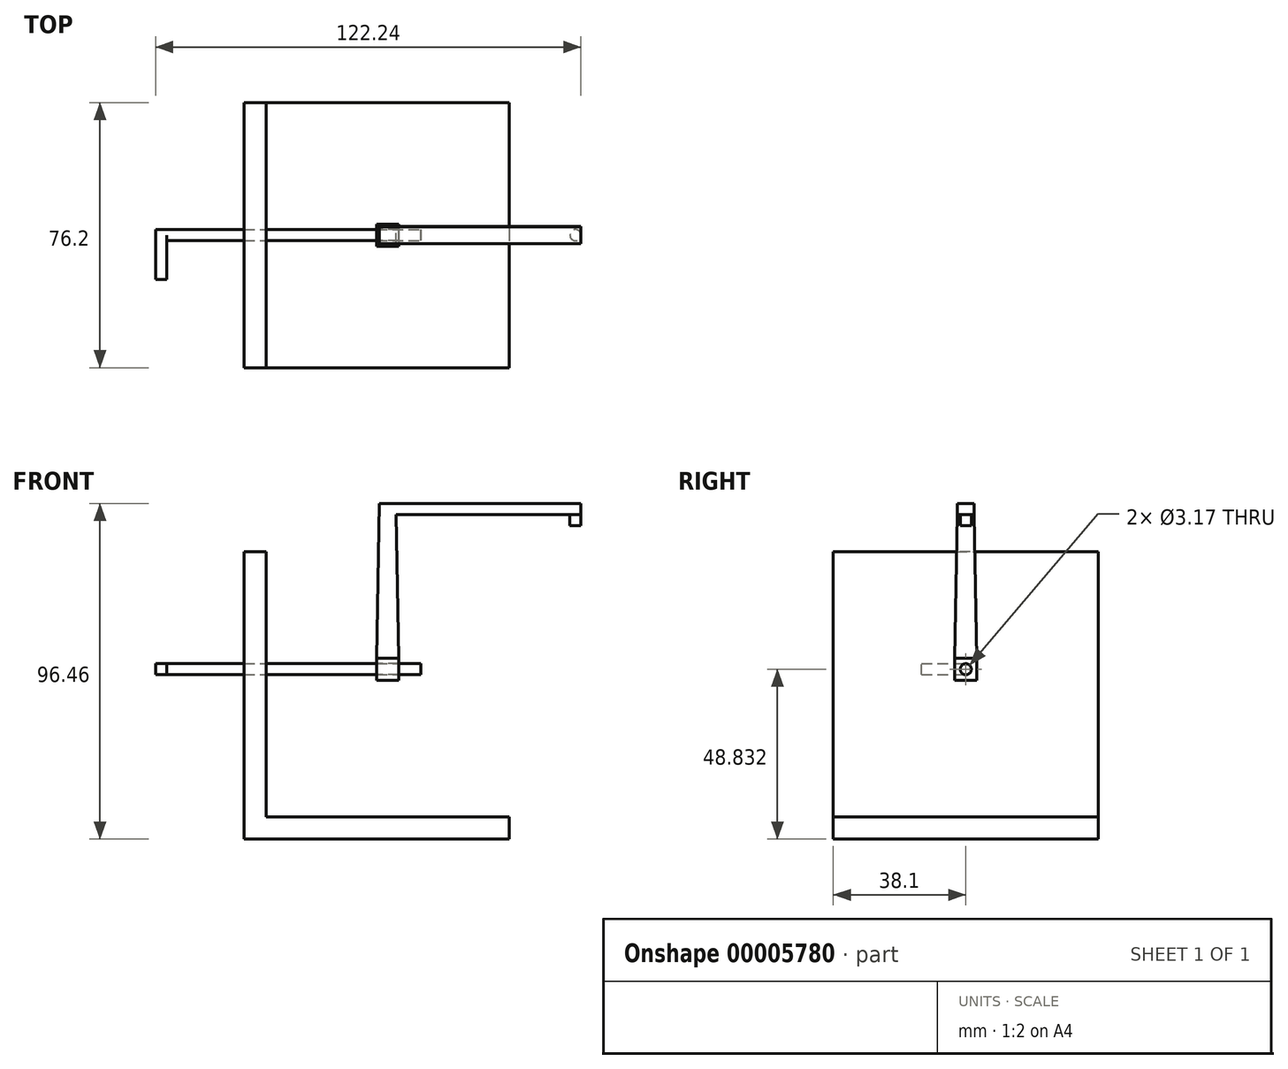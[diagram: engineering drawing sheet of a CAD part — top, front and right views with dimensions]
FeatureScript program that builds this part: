
annotation { "Feature Type Name" : "Feature", "Feature Type Description" : "" }
export const myFeature = defineFeature(function(context is Context, id is Id, definition is map)
    precondition{}
    {
        {
            var Q0;
            Q0=qCreatedBy(makeId("Top.planeOp"),FACE);
            var sketch = newSketch(context, id + "F0", { "sketchPlane" : qUnion([Q0])});
            skLineSegment(sketch, "E0.bottom", {"start": v(38.1, 38.1) * mm, "end": v(-38.1, 38.1) * mm});
            skLineSegment(sketch, "E0.top", {"start": v(38.1, -38.1) * mm, "end": v(-38.1, -38.1) * mm});
            skLineSegment(sketch, "E0.left", {"start": v(38.1, 38.1) * mm, "end": v(38.1, -38.1) * mm});
            skLineSegment(sketch, "E0.right", {"start": v(-38.1, 38.1) * mm, "end": v(-38.1, -38.1) * mm});
            skPoint(sketch, "E0.middle", {"position": v(0, 0) * mm});
            skSolve(sketch);
        }
        {
            var Q0;
            Q0=makeQuery(id+"F0.imprint","IMPRINT",FACE,{"disambiguationData":[TD([[makeQuery(id+"F0.imprint","IMPRINT",EDGE,{"derivedFrom":sQuery(id+"F0.wireOp",EDGE,"E0.bottom")}),1.0]])]});
            extrude(context, id + "F1", {"entities" : qUnion([Q0]), "depth" : 6.35 * mm});
        }
        {
            var Q0;
            Q0=makeQuery(id+"F1.opExtrude","CAP_FACE",FACE,{"disambiguationData":[OSD([sQuery(id+"F0.wireOp",EDGE,"E0.bottom"),sQuery(id+"F0.wireOp",EDGE,"E0.top"),sQuery(id+"F0.wireOp",EDGE,"E0.left"),sQuery(id+"F0.wireOp",EDGE,"E0.right")])],"isStart":false});
            var sketch = newSketch(context, id + "F2", { "sketchPlane" : qUnion([Q0])});
            skLineSegment(sketch, "E1.bottom", {"start": v(-38.1, -38.1) * mm, "end": v(-31.75, -38.1) * mm});
            skLineSegment(sketch, "E1.top", {"start": v(-38.1, 38.1) * mm, "end": v(-31.75, 38.1) * mm});
            skLineSegment(sketch, "E1.left", {"start": v(-38.1, -38.1) * mm, "end": v(-38.1, 38.1) * mm});
            skLineSegment(sketch, "E1.right", {"start": v(-31.75, -38.1) * mm, "end": v(-31.75, 38.1) * mm});
            skSolve(sketch);
        }
        {
            var Q0;
            Q0=makeQuery(id+"F2.imprint","IMPRINT",FACE,{"disambiguationData":[TD([[makeQuery(id+"F2.imprint","IMPRINT",EDGE,{"derivedFrom":sQuery(id+"F2.wireOp",EDGE,"E1.bottom")}),-1.0]])]});
            extrude(context, id + "F3", {"entities" : qUnion([Q0]), "operationType" : NewBodyOperationType.ADD, "depth" : 76.2 * mm});
        }
        {
            var Q0;
            Q0=makeQuery(id+"F3.boolean.opBoolean","MERGE",FACE,{"derivedFrom":[makeQuery(id+"F1.opExtrude","SWEPT_FACE",FACE,{"disambiguationData":[OSD([sQuery(id+"F0.wireOp",EDGE,"E0.right")])]}),makeQuery(id+"F3.opExtrude","SWEPT_FACE",FACE,{"disambiguationData":[OSD([sQuery(id+"F2.wireOp",EDGE,"E1.left")])]})]});
            var sketch = newSketch(context, id + "F4", { "sketchPlane" : qUnion([Q0])});
            skCircle(sketch, "E2", {"center": v(0, 48.83) * mm, "radius": 1.59 * mm});
            skPoint(sketch, "E2.centerSnap0", {"position": v(0, 82.55) * mm});
            skSolve(sketch);
        }
        {
            var Q0;
            Q0=makeQuery(id+"F4.imprint","IMPRINT",FACE,{"disambiguationData":[TD([[makeQuery(id+"F4.imprint","IMPRINT",EDGE,{"derivedFrom":sQuery(id+"F4.wireOp",EDGE,"E2")}),1.0]])]});
            extrude(context, id + "F5", {"entities" : qUnion([Q0]), "operationType" : NewBodyOperationType.REMOVE, "oppositeDirection" : true, "depth" : 25.4 * mm});
        }
        {
            var Q0;
            Q0 = qSketchRegion(id + "F4", true);
            extrude(context, id + "F6", {"entities" : qUnion([Q0]), "depth" : 25.4 * mm, "hasSecondDirection" : true, "secondDirectionOppositeDirection" : true, "secondDirectionDepth" : 50.8 * mm});
        }
        {
            var Q0;
            Q0=qCreatedBy(makeId("Front.planeOp"),FACE);
            var sketch = newSketch(context, id + "F7", { "sketchPlane" : qUnion([Q0])});
            skLineSegment(sketch, "E3.0", {"start": v(-63.5, 47.24) * mm, "end": v(-63.5, 50.42) * mm});
            skPoint(sketch, "E4.orphan", {"position": v(-38.1, 0) * mm});
            skPoint(sketch, "E5.orphan", {"position": v(-38.1, 82.55) * mm});
            skLineSegment(sketch, "E6", {"start": v(-60.33, 50.42) * mm, "end": v(-60.33, 47.24) * mm});
            skLineSegment(sketch, "E7", {"start": v(-63.5, 50.42) * mm, "end": v(-60.33, 50.42) * mm});
            skLineSegment(sketch, "E8", {"start": v(-60.33, 47.24) * mm, "end": v(-63.5, 47.24) * mm});
            skSolve(sketch);
        }
        {
            var Q0;
            Q0 = qSketchRegion(id + "F7", true);
            extrude(context, id + "F8", {"entities" : qUnion([Q0]), "operationType" : NewBodyOperationType.ADD, "depth" : 12.7 * mm});
        }
        {
            var Q0;
            Q0=qCreatedBy(makeId("Right.planeOp"),FACE);
            var sketch = newSketch(context, id + "F9", { "sketchPlane" : qUnion([Q0])});
            skCircle(sketch, "E9.0", {"center": v(0, 48.83) * mm, "radius": 1.59 * mm});
            skLineSegment(sketch, "E10.bottom", {"start": v(3.18, 45.66) * mm, "end": v(-3.17, 45.66) * mm});
            skLineSegment(sketch, "E10.top", {"start": v(3.18, 52) * mm, "end": v(-3.17, 52) * mm});
            skLineSegment(sketch, "E10.left", {"start": v(3.18, 45.66) * mm, "end": v(3.18, 52) * mm});
            skLineSegment(sketch, "E10.right", {"start": v(-3.17, 45.66) * mm, "end": v(-3.17, 52) * mm});
            skSolve(sketch);
        }
        {
            var Q0;
            Q0=makeQuery(id+"F9.imprint","IMPRINT",FACE,{"disambiguationData":[TD([[makeQuery(id+"F9.imprint","IMPRINT",EDGE,{"derivedFrom":sQuery(id+"F9.wireOp",EDGE,"E9.0")}),-1.0]])]});
            extrude(context, id + "F10", {"entities" : qUnion([Q0]), "depth" : 6.35 * mm});
        }
        {
            var Q0;
            Q0=makeQuery(id+"F10.opExtrude","SWEPT_FACE",FACE,{"disambiguationData":[OSD([sQuery(id+"F9.wireOp",EDGE,"E10.top")])]});
            extrude(context, id + "F11", {"entities" : qUnion([Q0]), "operationType" : NewBodyOperationType.ADD, "depth" : 44.45 * mm, "hasDraft" : true, "draftAngle" : 1 * degree, "draftPullDirection" : true});
        }
        {
            var Q0;
            Q0=qCreatedBy(makeId("Right.planeOp"),FACE);
            var sketch = newSketch(context, id + "F12", { "sketchPlane" : qUnion([Q0])});
            skPoint(sketch, "E11.0", {"position": v(0, 96.46) * mm});
            skLineSegment(sketch, "E12.0", {"start": v(2.4, 96.46) * mm, "end": v(-2.4, 96.46) * mm});
            skLineSegment(sketch, "E13.0", {"start": v(-2.4, 96.46) * mm, "end": v(-2.45, 93.28) * mm});
            skLineSegment(sketch, "E14.0", {"start": v(2.4, 96.46) * mm, "end": v(2.45, 93.28) * mm});
            skLineSegment(sketch, "E15", {"start": v(2.45, 93.28) * mm, "end": v(-2.45, 93.28) * mm});
            skPoint(sketch, "E16.orphan", {"position": v(3.18, 52) * mm});
            skPoint(sketch, "E17.orphan", {"position": v(-3.17, 52) * mm});
            skSolve(sketch);
        }
        {
            var Q0;
            Q0=makeQuery(id+"F12.imprint","IMPRINT",FACE,{"disambiguationData":[TD([[makeQuery(id+"F12.imprint","IMPRINT",EDGE,{"derivedFrom":sQuery(id+"F12.wireOp",EDGE,"E12.0")}),1.0]])]});
            extrude(context, id + "F13", {"entities" : qUnion([Q0]), "operationType" : NewBodyOperationType.ADD, "depth" : 58.74 * mm, "hasSecondDirection" : true, "secondDirectionOppositeDirection" : false, "secondDirectionDepth" : 2.54 * mm});
        }
        {
            var Q0;
            Q0=makeQuery(id+"F13.opExtrude","SWEPT_FACE",FACE,{"disambiguationData":[OSD([sQuery(id+"F12.wireOp",EDGE,"E15")])]});
            var sketch = newSketch(context, id + "F14", { "sketchPlane" : qUnion([Q0])});
            skLineSegment(sketch, "E18.0", {"start": v(57.15, -2.45) * mm, "end": v(57.15, 2.45) * mm, "construction": true});
            skCircle(sketch, "E19", {"center": v(57.15, 0) * mm, "radius": 1.59 * mm});
            skSolve(sketch);
        }
        {
            var Q0;
            Q0=makeQuery(id+"F14.imprint","IMPRINT",FACE,{"disambiguationData":[TD([[makeQuery(id+"F14.imprint","IMPRINT",EDGE,{"derivedFrom":sQuery(id+"F14.wireOp",EDGE,"E19")}),1.0]])]});
            extrude(context, id + "F15", {"entities" : qUnion([Q0]), "operationType" : NewBodyOperationType.ADD, "depth" : 3.17 * mm});
        }
    });
